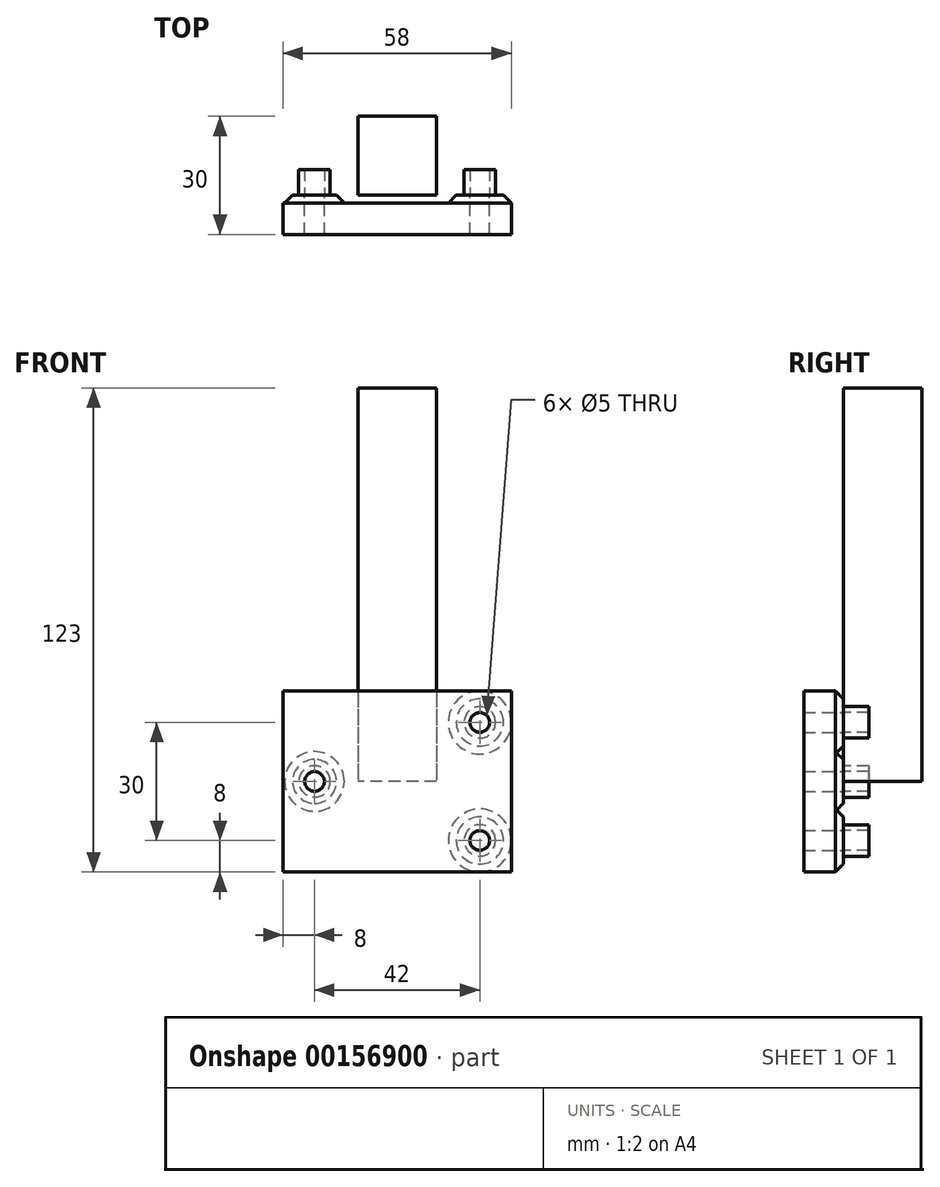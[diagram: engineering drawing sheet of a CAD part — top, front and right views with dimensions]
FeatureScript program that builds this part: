
annotation { "Feature Type Name" : "Feature", "Feature Type Description" : "" }
export const myFeature = defineFeature(function(context is Context, id is Id, definition is map)
    precondition{}
    {
        {
            var Q0;
            Q0=qCreatedBy(makeId("Front.planeOp"),FACE);
            cPlane(context, id + "F0", {"entities" : qUnion([Q0]), "cplaneType" : CPlaneType.OFFSET, "offset" : 12 * mm, "width" : 150 * mm, "height" : 150 * mm});
        }
        {
            var Q0;
            Q0=qCreatedBy(makeId("Top.planeOp"),FACE);
            var sketch = newSketch(context, id + "F1", { "sketchPlane" : qUnion([Q0])});
            skLineSegment(sketch, "E0.bottom", {"start": v(10, -10) * mm, "end": v(-10, -10) * mm});
            skLineSegment(sketch, "E0.top", {"start": v(10, 10) * mm, "end": v(-10, 10) * mm});
            skLineSegment(sketch, "E0.left", {"start": v(10, -10) * mm, "end": v(10, 10) * mm});
            skLineSegment(sketch, "E0.right", {"start": v(-10, -10) * mm, "end": v(-10, 10) * mm});
            skPoint(sketch, "E0.middle", {"position": v(0, 0) * mm});
            skSolve(sketch);
        }
        {
            var Q0;
            Q0 = qSketchRegion(id + "F1", true);
            extrude(context, id + "F2", {"entities" : qUnion([Q0]), "depth" : 100 * mm, "offsetDistance" : 25 * mm});
        }
        {
            var Q0;
            Q0=qCreatedBy(id+"F0.planeOp",FACE);
            var sketch = newSketch(context, id + "F3", { "sketchPlane" : qUnion([Q0])});
            skLineSegment(sketch, "E1.bottom", {"start": v(-29, -23) * mm, "end": v(29, -23) * mm});
            skLineSegment(sketch, "E1.top", {"start": v(-29, 23) * mm, "end": v(29, 23) * mm});
            skLineSegment(sketch, "E1.left", {"start": v(-29, -23) * mm, "end": v(-29, 23) * mm});
            skLineSegment(sketch, "E1.right", {"start": v(29, -23) * mm, "end": v(29, 23) * mm});
            skPoint(sketch, "E1.middle", {"position": v(0, 0) * mm});
            skCircle(sketch, "E2", {"center": v(-21, 0) * mm, "radius": 2.5 * mm});
            skCircle(sketch, "E3", {"center": v(21, 15) * mm, "radius": 2.5 * mm});
            skCircle(sketch, "E4", {"center": v(21, -15) * mm, "radius": 2.5 * mm});
            skLineSegment(sketch, "E5", {"start": v(29, 0) * mm, "end": v(-29, 0) * mm, "construction": true});
            skSolve(sketch);
        }
        {
            var Q0;
            Q0=makeQuery(id+"F3.imprint","IMPRINT",FACE,{"disambiguationData":[TD([[makeQuery(id+"F3.imprint","IMPRINT",EDGE,{"derivedFrom":sQuery(id+"F3.wireOp",EDGE,"E1.bottom")}),1.0]])]});
            extrude(context, id + "F4", {"entities" : qUnion([Q0]), "depth" : 8 * mm, "offsetDistance" : 25 * mm});
        }
        {
            var Q0;
            Q0=makeQuery(id+"F4.opExtrude","CAP_FACE",FACE,{"disambiguationData":[OSD([sQuery(id+"F3.wireOp",EDGE,"E1.bottom"),sQuery(id+"F3.wireOp",EDGE,"E1.top"),sQuery(id+"F3.wireOp",EDGE,"E1.left"),sQuery(id+"F3.wireOp",EDGE,"E1.right"),sQuery(id+"F3.wireOp",EDGE,"E2"),sQuery(id+"F3.wireOp",EDGE,"E3"),sQuery(id+"F3.wireOp",EDGE,"E4")])],"isStart":true});
            var sketch = newSketch(context, id + "F5", { "sketchPlane" : qUnion([Q0])});
            skCircle(sketch, "E6", {"center": v(-21, 15) * mm, "radius": 8 * mm});
            skCircle(sketch, "E7", {"center": v(-21, 15) * mm, "radius": 2.5 * mm});
            skCircle(sketch, "E8", {"center": v(-21, -15) * mm, "radius": 8 * mm});
            skCircle(sketch, "E9", {"center": v(-21, -15) * mm, "radius": 2.5 * mm});
            skCircle(sketch, "E10", {"center": v(21, 0) * mm, "radius": 2.5 * mm});
            skCircle(sketch, "E11", {"center": v(21, 0) * mm, "radius": 7.58 * mm});
            skSolve(sketch);
        }
        {
            var Q0;
            Q0 = qSketchRegion(id + "F5", true);
            extrude(context, id + "F6", {"entities" : qUnion([Q0]), "operationType" : NewBodyOperationType.ADD, "depth" : 2 * mm, "offsetDistance" : 25 * mm});
        }
        {
            var Q0;
            Q0=makeQuery(id+"F6.opExtrude","CAP_EDGE",EDGE,{"disambiguationData":[OSD([sQuery(id+"F5.wireOp",EDGE,"E6")])],"isStart":false});
            var Q1;
            Q1=makeQuery(id+"F6.opExtrude","CAP_EDGE",EDGE,{"disambiguationData":[OSD([sQuery(id+"F5.wireOp",EDGE,"E11")])],"isStart":false});
            var Q2;
            Q2=makeQuery(id+"F6.opExtrude","CAP_EDGE",EDGE,{"disambiguationData":[OSD([sQuery(id+"F5.wireOp",EDGE,"E8")])],"isStart":false});
            chamfer(context, id + "F7", {"entities" : qUnion([Q0, Q1, Q2]), "width" : 2 * mm, "tangentPropagation" : true});
        }
        {
            var Q0;
            Q0=makeQuery(id+"F6.opExtrude","CAP_FACE",FACE,{"disambiguationData":[OSD([sQuery(id+"F5.wireOp",EDGE,"E6"),sQuery(id+"F5.wireOp",EDGE,"E7")])],"isStart":false});
            var sketch = newSketch(context, id + "F8", { "sketchPlane" : qUnion([Q0])});
            skCircle(sketch, "E12", {"center": v(-21, 15) * mm, "radius": 4 * mm});
            skCircle(sketch, "E13", {"center": v(-21, 15) * mm, "radius": 2.5 * mm});
            skCircle(sketch, "E14", {"center": v(21, 0) * mm, "radius": 4 * mm});
            skCircle(sketch, "E15", {"center": v(21, 0) * mm, "radius": 2.5 * mm});
            skCircle(sketch, "E16", {"center": v(-21, -15) * mm, "radius": 4 * mm});
            skCircle(sketch, "E17", {"center": v(-21, -15) * mm, "radius": 2.5 * mm});
            skSolve(sketch);
        }
        {
            var Q0;
            Q0 = qSketchRegion(id + "F8", true);
            extrude(context, id + "F9", {"entities" : qUnion([Q0]), "depth" : 6.5 * mm, "offsetDistance" : 25 * mm});
        }
    });
